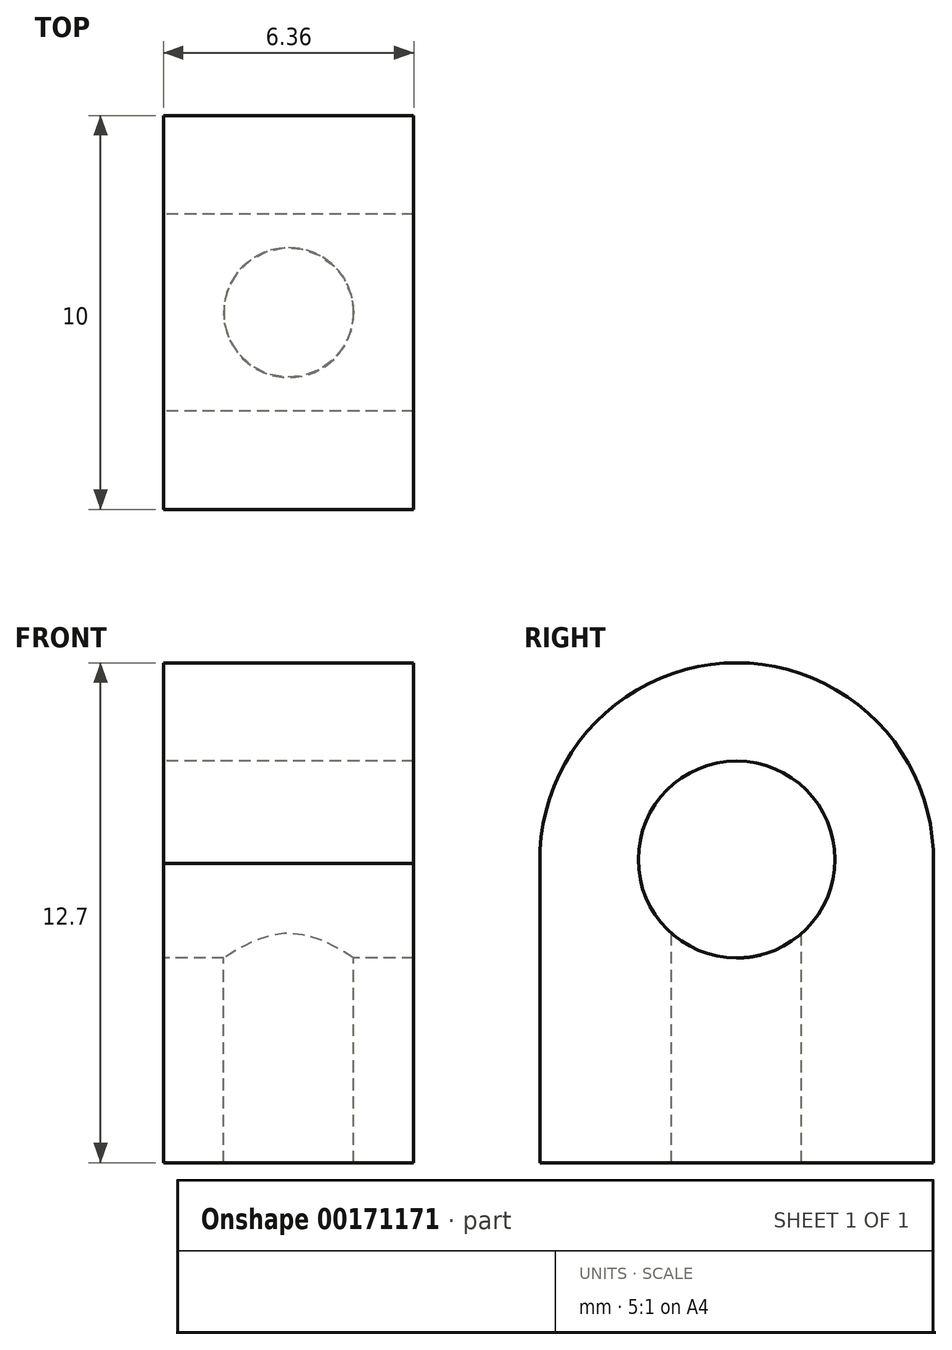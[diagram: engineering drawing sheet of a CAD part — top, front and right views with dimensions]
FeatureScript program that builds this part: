
annotation { "Feature Type Name" : "Feature", "Feature Type Description" : "" }
export const myFeature = defineFeature(function(context is Context, id is Id, definition is map)
    precondition{}
    {
        {
            var Q0;
            Q0=qCreatedBy(makeId("Right.planeOp"),FACE);
            var sketch = newSketch(context, id + "F0", { "sketchPlane" : qUnion([Q0])});
            skArc(sketch, "E0", {"start": v(5, -0.1) * mm, "mid": v(0, 5) * mm, "end": v(-5, -0.1) * mm});
            skLineSegment(sketch, "E1.bottom", {"start": v(-5, -0.1) * mm, "end": v(-5, -0.1) * mm});
            skLineSegment(sketch, "E1.top", {"start": v(-5, -7.7) * mm, "end": v(5, -7.7) * mm});
            skLineSegment(sketch, "E1.left", {"start": v(-5, -0.1) * mm, "end": v(-5, -7.7) * mm});
            skLineSegment(sketch, "E1.right", {"start": v(5, -0.1) * mm, "end": v(5, -7.7) * mm});
            skPoint(sketch, "E1.middle", {"position": v(0, -3.9) * mm});
            skLineSegment(sketch, "E2.trimOffspring", {"start": v(5, -0.1) * mm, "end": v(5, -0.1) * mm});
            skSolve(sketch);
        }
        {
            var Q0;
            {var subQ0=sQuery(id+"F0.wireOp",EDGE,"E0");Q0=makeQuery(id+"F0.imprint","IMPRINT",FACE,{"disambiguationData":[TD([[makeQuery(id+"F0.imprint","IMPRINT",EDGE,{"derivedFrom":subQ0}),1.0]])]});}
            var Q1;
            Q1=makeQuery(id+"F0.imprint","IMPRINT",FACE,{"disambiguationData":[TD([[makeQuery(id+"F0.imprint","IMPRINT",EDGE,{"derivedFrom":sQuery(id+"F0.wireOp",EDGE,"E1.top")}),1.0]])]});
            extrude(context, id + "F1", {"entities" : qUnion([Q0, Q1]), "depth" : 6.35 * mm, "symmetric" : true});
        }
        {
            var Q0;
            Q0=makeQuery(id+"F1.opExtrude","CAP_FACE",FACE,{"disambiguationData":[OSD([sQuery(id+"F0.wireOp",EDGE,"E0"),sQuery(id+"F0.wireOp",EDGE,"E1.bottom"),sQuery(id+"F0.wireOp",EDGE,"E1.top"),sQuery(id+"F0.wireOp",EDGE,"E1.left"),sQuery(id+"F0.wireOp",EDGE,"E1.right"),sQuery(id+"F0.wireOp",EDGE,"E2.trimOffspring")])],"isStart":false});
            var sketch = newSketch(context, id + "F2", { "sketchPlane" : qUnion([Q0])});
            skPoint(sketch, "E3", {"position": v(0, 0) * mm});
            skSolve(sketch);
        }
        {
            var Q0;
            Q0=sQuery(id+"F2.wireOp",VERTEX,"E3");
            var Q1;
            Q1=makeQuery(id+"F1.opExtrude","SWEPT_BODY",BODY,{"disambiguationData":[OSD([sQuery(id+"F0.wireOp",EDGE,"E0"),sQuery(id+"F0.wireOp",EDGE,"E1.bottom"),sQuery(id+"F0.wireOp",EDGE,"E1.top"),sQuery(id+"F0.wireOp",EDGE,"E1.left"),sQuery(id+"F0.wireOp",EDGE,"E1.right"),sQuery(id+"F0.wireOp",EDGE,"E2.trimOffspring")])]});
            hole(context, id + "F3", {"style" : HoleStyle.SIMPLE, "endStyle" : HoleEndStyle.THROUGH, "standardTappedOrClearance" : lookupTablePath({ "standard" : "ISO", "engagement" : "75%", "pitch" : "1 mm", "size" : "M6", "type" : "Tapped" }), "standardBlindInLast" : lookupTablePath({ "standard" : "ISO", "engagement" : "75%", "pitch" : "1 mm", "size" : "M6", "type" : "Tapped" }), "holeDiameter" : 5 * mm, "locations" : qUnion([Q0]), "scope" : qUnion([Q1]), "isTappedThrough" : true, "majorDiameter" : 6 * mm, "showTappedDepth" : true});
        }
        {
            var Q0;
            Q0=makeQuery(id+"F1.opExtrude","SWEPT_FACE",FACE,{"disambiguationData":[OSD([sQuery(id+"F0.wireOp",EDGE,"E1.top")])]});
            var sketch = newSketch(context, id + "F4", { "sketchPlane" : qUnion([Q0])});
            skPoint(sketch, "E4", {"position": v(0, 0) * mm});
            skSolve(sketch);
        }
        {
            var Q0;
            Q0=sQuery(id+"F4.wireOp",VERTEX,"E4");
            var Q1;
            Q1=makeQuery(id+"F1.opExtrude","SWEPT_BODY",BODY,{"disambiguationData":[OSD([sQuery(id+"F0.wireOp",EDGE,"E0"),sQuery(id+"F0.wireOp",EDGE,"E1.bottom"),sQuery(id+"F0.wireOp",EDGE,"E1.top"),sQuery(id+"F0.wireOp",EDGE,"E1.left"),sQuery(id+"F0.wireOp",EDGE,"E1.right"),sQuery(id+"F0.wireOp",EDGE,"E2.trimOffspring")])]});
            hole(context, id + "F5", {"style" : HoleStyle.SIMPLE, "endStyle" : HoleEndStyle.BLIND, "standardTappedOrClearance" : lookupTablePath({ "standard" : "ISO", "fit" : "Normal", "size" : "M3", "type" : "Clearance" }), "standardBlindInLast" : lookupTablePath({ "fit" : "Standard", "standard" : "ISO", "size" : "M3", "type" : "Clearance" }), "holeDiameter" : 3.3 * mm, "holeDepth" : 6 * mm, "locations" : qUnion([Q0]), "scope" : qUnion([Q1])});
        }
    });
